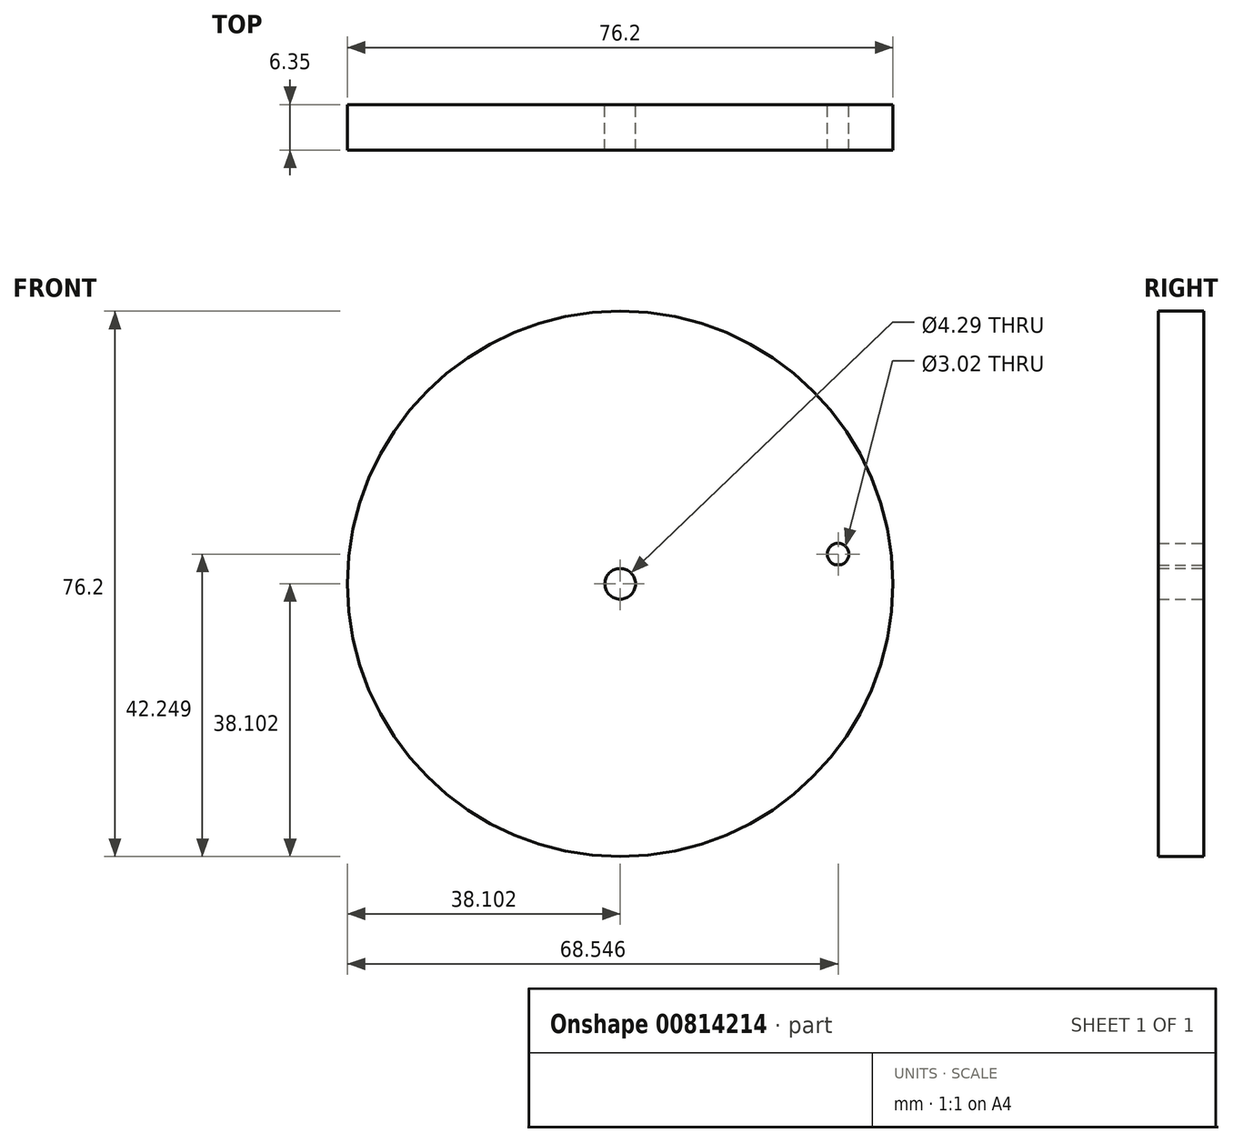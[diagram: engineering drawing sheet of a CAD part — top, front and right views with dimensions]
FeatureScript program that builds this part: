
annotation { "Feature Type Name" : "Feature", "Feature Type Description" : "" }
export const myFeature = defineFeature(function(context is Context, id is Id, definition is map)
    precondition{}
    {
        {
            var Q0;
            Q0=qCreatedBy(makeId("Front.planeOp"),FACE);
            var sketch = newSketch(context, id + "F0", { "sketchPlane" : qUnion([Q0])});
            skCircle(sketch, "E0", {"center": v(-19.48, 26.34) * mm, "radius": 38.1 * mm});
            skCircle(sketch, "E1", {"center": v(-19.48, 26.34) * mm, "radius": 2.15 * mm});
            skCircle(sketch, "E2", {"center": v(10.97, 30.49) * mm, "radius": 1.51 * mm});
            skSolve(sketch);
        }
        {
            var Q0;
            Q0=makeQuery(id+"F0.imprint","IMPRINT",FACE,{"disambiguationData":[TD([[makeQuery(id+"F0.imprint","IMPRINT",EDGE,{"derivedFrom":sQuery(id+"F0.wireOp",EDGE,"E0")}),1.0]])]});
            extrude(context, id + "F1", {"entities" : qUnion([Q0]), "depth" : 6.35 * mm, "offsetDistance" : 25.4 * mm});
        }
    });
